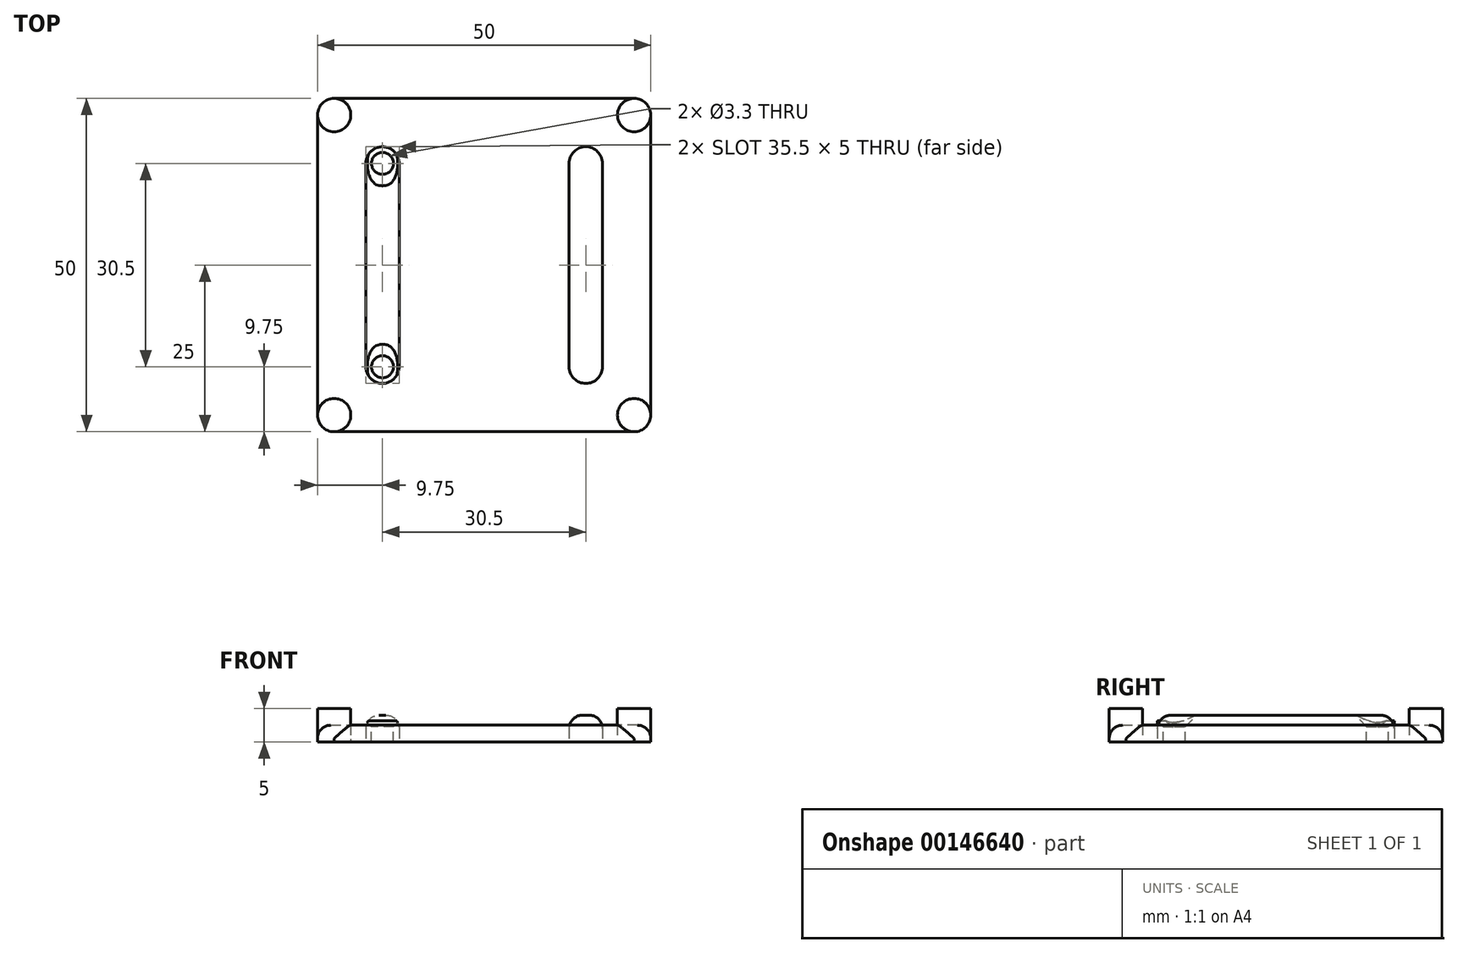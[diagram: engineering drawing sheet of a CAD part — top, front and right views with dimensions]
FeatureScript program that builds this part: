
annotation { "Feature Type Name" : "Feature", "Feature Type Description" : "" }
export const myFeature = defineFeature(function(context is Context, id is Id, definition is map)
    precondition{}
    {
        {
            var Q0;
            Q0=qCreatedBy(makeId("Top.planeOp"),FACE);
            var sketch = newSketch(context, id + "F0", { "sketchPlane" : qUnion([Q0])});
            skPoint(sketch, "E0.middle", {"position": v(0, 0) * mm});
            skCircle(sketch, "E1", {"center": v(-22.5, 22.5) * mm, "radius": 2.5 * mm});
            skCircle(sketch, "E2", {"center": v(22.5, 22.5) * mm, "radius": 2.5 * mm});
            skCircle(sketch, "E3", {"center": v(22.5, -22.5) * mm, "radius": 2.5 * mm});
            skCircle(sketch, "E4", {"center": v(-22.5, -22.5) * mm, "radius": 2.5 * mm});
            skArc(sketch, "E5", {"start": v(-17.75, -15.25) * mm, "mid": v(-15.25, -17.75) * mm, "end": v(-12.75, -15.25) * mm});
            skArc(sketch, "E6", {"start": v(12.75, -15.25) * mm, "mid": v(15.25, -17.75) * mm, "end": v(17.75, -15.25) * mm});
            skArc(sketch, "E7", {"start": v(17.75, 15.25) * mm, "mid": v(15.25, 17.75) * mm, "end": v(12.75, 15.25) * mm});
            skArc(sketch, "E8", {"start": v(-12.75, 15.25) * mm, "mid": v(-15.25, 17.75) * mm, "end": v(-17.75, 15.25) * mm});
            skLineSegment(sketch, "E9", {"start": v(-22.5, 25) * mm, "end": v(22.5, 25) * mm});
            skLineSegment(sketch, "E10", {"start": v(25, 22.5) * mm, "end": v(25, -22.5) * mm});
            skLineSegment(sketch, "E11", {"start": v(22.5, -25) * mm, "end": v(-22.5, -25) * mm});
            skLineSegment(sketch, "E12", {"start": v(-25, -22.5) * mm, "end": v(-25, 22.5) * mm});
            skLineSegment(sketch, "E13", {"start": v(-17.75, 15.25) * mm, "end": v(-17.75, -15.25) * mm});
            skLineSegment(sketch, "E14", {"start": v(17.75, -15.25) * mm, "end": v(17.75, 15.25) * mm});
            skLineSegment(sketch, "E15", {"start": v(12.75, 15.25) * mm, "end": v(12.75, -15.25) * mm});
            skLineSegment(sketch, "E16", {"start": v(-12.75, 15.25) * mm, "end": v(-12.75, -15.25) * mm});
            skLineSegment(sketch, "E17", {"start": v(-22.5, 22.5) * mm, "end": v(22.5, -22.5) * mm, "construction": true});
            skLineSegment(sketch, "E18", {"start": v(-22.5, -22.5) * mm, "end": v(22.5, 22.5) * mm, "construction": true});
            skSolve(sketch);
        }
        {
            var Q0;
            {var subQ0=sQuery(id+"F0.wireOp",EDGE,"E4");var subQ1=makeQuery(id+"F0.imprint","INTERSECT",VERTEX,{"derivedFrom":[subQ0,sQuery(id+"F0.wireOp",EDGE,"E11")]});Q0=makeQuery(id+"F0.imprint","IMPRINT",FACE,{"disambiguationData":[TD([[makeQuery(id+"F0.imprint","IMPRINT",EDGE,{"disambiguationData":[TD([[subQ1,1.0]])],"derivedFrom":subQ0}),1.0]])]});}
            var Q1;
            {var subQ0=sQuery(id+"F0.wireOp",EDGE,"E3");var subQ1=makeQuery(id+"F0.imprint","INTERSECT",VERTEX,{"derivedFrom":[subQ0,sQuery(id+"F0.wireOp",EDGE,"E10")]});Q1=makeQuery(id+"F0.imprint","IMPRINT",FACE,{"disambiguationData":[TD([[makeQuery(id+"F0.imprint","IMPRINT",EDGE,{"disambiguationData":[TD([[subQ1,-1.0]])],"derivedFrom":subQ0}),1.0]])]});}
            var Q2;
            {var subQ0=sQuery(id+"F0.wireOp",EDGE,"E2");var subQ1=makeQuery(id+"F0.imprint","INTERSECT",VERTEX,{"derivedFrom":[subQ0,sQuery(id+"F0.wireOp",EDGE,"E9")]});Q2=makeQuery(id+"F0.imprint","IMPRINT",FACE,{"disambiguationData":[TD([[makeQuery(id+"F0.imprint","IMPRINT",EDGE,{"disambiguationData":[TD([[subQ1,1.0]])],"derivedFrom":subQ0}),1.0]])]});}
            var Q3;
            {var subQ0=sQuery(id+"F0.wireOp",EDGE,"E1");var subQ1=makeQuery(id+"F0.imprint","INTERSECT",VERTEX,{"derivedFrom":[subQ0,sQuery(id+"F0.wireOp",EDGE,"E9")]});Q3=makeQuery(id+"F0.imprint","IMPRINT",FACE,{"disambiguationData":[TD([[makeQuery(id+"F0.imprint","IMPRINT",EDGE,{"disambiguationData":[TD([[subQ1,-1.0]])],"derivedFrom":subQ0}),1.0]])]});}
            extrude(context, id + "F1", {"entities" : qUnion([Q0, Q1, Q2, Q3]), "depth" : 5 * mm});
        }
        {
            var Q0;
            Q0=makeQuery(id+"F0.imprint","IMPRINT",FACE,{"disambiguationData":[TD([[makeQuery(id+"F0.imprint","IMPRINT",EDGE,{"derivedFrom":sQuery(id+"F0.wireOp",EDGE,"E5")}),1.0]])]});
            var Q1;
            Q1=makeQuery(id+"F0.imprint","IMPRINT",FACE,{"disambiguationData":[TD([[makeQuery(id+"F0.imprint","IMPRINT",EDGE,{"derivedFrom":sQuery(id+"F0.wireOp",EDGE,"E6")}),1.0]])]});
            extrude(context, id + "F2", {"entities" : qUnion([Q0, Q1]), "depth" : 4 * mm});
        }
        {
            var Q0;
            Q0=makeQuery(id+"F0.imprint","IMPRINT",FACE,{"disambiguationData":[TD([[makeQuery(id+"F0.imprint","IMPRINT",EDGE,{"derivedFrom":sQuery(id+"F0.wireOp",EDGE,"E5")}),-1.0]])]});
            extrude(context, id + "F3", {"entities" : qUnion([Q0]), "depth" : 2.5 * mm});
        }
        {
            var Q0;
            Q0=sQuery(id+"F0.wireOp",VERTEX,"E1.center");
            var Q1;
            Q1=sQuery(id+"F0.wireOp",VERTEX,"E2.center");
            var Q2;
            Q2=sQuery(id+"F0.wireOp",VERTEX,"E3.center");
            var Q3;
            Q3=sQuery(id+"F0.wireOp",VERTEX,"E4.center");
            var Q4;
            Q4=makeQuery(id+"F2.opExtrude","SWEPT_BODY",BODY,{"disambiguationData":[OSD([sQuery(id+"F0.wireOp",EDGE,"E5"),sQuery(id+"F0.wireOp",EDGE,"E8"),sQuery(id+"F0.wireOp",EDGE,"E13"),sQuery(id+"F0.wireOp",EDGE,"E16")])]});
            hole(context, id + "F4", {"style" : HoleStyle.SIMPLE, "endStyle" : HoleEndStyle.THROUGH, "oppositeDirection" : true, "holeDiameter" : 2 * mm, "locations" : qUnion([Q0, Q1, Q2, Q3]), "scope" : qUnion([Q4]), "isTappedThrough" : true});
        }
        {
            var Q0;
            Q0=makeQuery(id+"F2.opExtrude","CAP_FACE",FACE,{"disambiguationData":[OSD([sQuery(id+"F0.wireOp",EDGE,"E5"),sQuery(id+"F0.wireOp",EDGE,"E8"),sQuery(id+"F0.wireOp",EDGE,"E13"),sQuery(id+"F0.wireOp",EDGE,"E16")])],"isStart":false});
            var sketch = newSketch(context, id + "F5", { "sketchPlane" : qUnion([Q0])});
            skPoint(sketch, "E19", {"position": v(-15.25, 15.25) * mm});
            skPoint(sketch, "E20", {"position": v(-15.25, -15.25) * mm});
            skPoint(sketch, "E21.0", {"position": v(15.25, 15.25) * mm});
            skPoint(sketch, "E22.0", {"position": v(15.25, -15.25) * mm});
            skSolve(sketch);
        }
        {
            var Q0;
            Q0=sQuery(id+"F5.wireOp",VERTEX,"E19");
            var Q1;
            Q1=sQuery(id+"F5.wireOp",VERTEX,"E20");
            var Q2;
            Q2=sQuery(id+"F5.wireOp",VERTEX,"11f08477-dec3-4f5f-a902-72d17bcef18e");
            var Q3;
            Q3=sQuery(id+"F5.wireOp",VERTEX,"d7b59594-2897-4982-93d0-b7494e559ce7");
            var Q4;
            Q4=sQuery(id+"F5.wireOp",VERTEX,"E21.0");
            var Q5;
            Q5=sQuery(id+"F5.wireOp",VERTEX,"E22.0");
            var Q6;
            Q6=makeQuery(id+"F2.opExtrude","SWEPT_BODY",BODY,{"disambiguationData":[OSD([sQuery(id+"F0.wireOp",EDGE,"E5"),sQuery(id+"F0.wireOp",EDGE,"E8"),sQuery(id+"F0.wireOp",EDGE,"E13"),sQuery(id+"F0.wireOp",EDGE,"E16")])]});
            hole(context, id + "F6", {"style" : HoleStyle.C_SINK, "endStyle" : HoleEndStyle.THROUGH, "standardTappedOrClearance" : lookupTablePath({ "standard" : "ISO", "fit" : "Normal", "size" : "M3", "type" : "Clearance" }), "standardBlindInLast" : lookupTablePath({ "fit" : "Standard", "standard" : "ISO", "size" : "M3", "type" : "Clearance" }), "holeDiameter" : 3.3 * mm, "cSinkDiameter" : 6.72 * mm, "cSinkAngle" : 90 * degree, "locations" : qUnion([Q0, Q1, Q2, Q3, Q4, Q5]), "scope" : qUnion([Q6]), "isTappedThrough" : true});
        }
        {
            var Q0;
            Q0=makeQuery(id+"F3.opExtrude","CAP_EDGE",EDGE,{"disambiguationData":[OSD([sQuery(id+"F0.wireOp",EDGE,"E11")])],"isStart":false});
            var Q1;
            Q1=makeQuery(id+"F3.opExtrude","CAP_EDGE",EDGE,{"disambiguationData":[OSD([sQuery(id+"F0.wireOp",EDGE,"E10")])],"isStart":false});
            var Q2;
            Q2=makeQuery(id+"F3.opExtrude","CAP_EDGE",EDGE,{"disambiguationData":[OSD([sQuery(id+"F0.wireOp",EDGE,"E12")])],"isStart":false});
            var Q3;
            Q3=makeQuery(id+"F3.opExtrude","CAP_EDGE",EDGE,{"disambiguationData":[OSD([sQuery(id+"F0.wireOp",EDGE,"E9")])],"isStart":false});
            var Q4;
            Q4=makeQuery(id+"F2.opExtrude","CAP_EDGE",EDGE,{"disambiguationData":[OSD([sQuery(id+"F0.wireOp",EDGE,"E13")])],"isStart":false});
            var Q5;
            Q5=makeQuery(id+"F2.opExtrude","CAP_EDGE",EDGE,{"disambiguationData":[OSD([sQuery(id+"F0.wireOp",EDGE,"E16")])],"isStart":false});
            var Q6;
            Q6=makeQuery(id+"F2.opExtrude","CAP_EDGE",EDGE,{"disambiguationData":[OSD([sQuery(id+"F0.wireOp",EDGE,"E15")])],"isStart":false});
            var Q7;
            Q7=makeQuery(id+"F2.opExtrude","CAP_EDGE",EDGE,{"disambiguationData":[OSD([sQuery(id+"F0.wireOp",EDGE,"E14")])],"isStart":false});
            fillet(context, id + "F7", {"entities" : qUnion([Q0, Q1, Q2, Q3, Q4, Q5, Q6, Q7]), "radius" : 2 * mm, "tangentPropagation" : true, "allowEdgeOverflow" : false});
        }
    });
